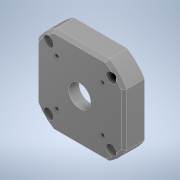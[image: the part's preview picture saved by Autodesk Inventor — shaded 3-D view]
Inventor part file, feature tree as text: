
AUTODESK INVENTOR PART (.ipt)
format: ipt  version: 2022 (Build 260153000, 153)  size: 179,712 bytes
history: mixed  units: in
note: dims shown in document units (in); Inventor stores cm internally (conversion verified against a paired STEP export)
features: extrude x2, sketch x2, chamfer x1, imported_body x1
ambient origin geometry x8: Origin, YZ Plane, XZ Plane, XY Plane, X Axis, Y Axis, Z Axis, Center Point
bodies: Solid1 (imported_parasolid)
feature tree (6):
  extrude  "Extrusion1"  Depth=0.3937in TaperAngle=0.0deg
  extrude  "Extrusion2"  Depth=0.3937in TaperAngle=0.0deg
  sketch  "Sketch1"  dims[d0=0.1102in d1=0.3937in d2=0.0in]
  sketch  "Sketch2"  dims[d3=0.5906in d4=0.3937in d5=0.0in]
  chamfer  "Chamfer2"  [1 undecoded]
  imported_body  NMx_Import_Brep_tag  [imported B-rep: ~32 faces, bbox_mm=[53.213203, 60.0, 14.0]]
note: 1 required parameter value undecoded (feature->parameter linkage not recoverable at this tier; creation-order binding heuristic only, values carry confidence <= 0.55)
